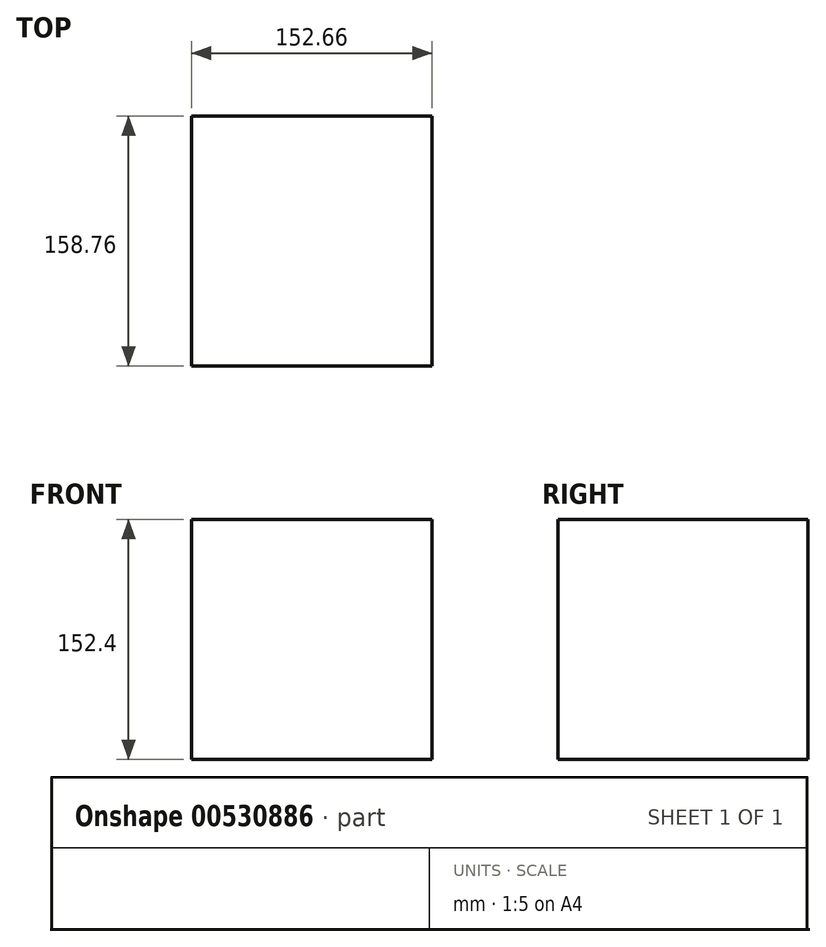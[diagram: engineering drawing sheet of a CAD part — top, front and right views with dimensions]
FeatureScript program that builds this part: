
annotation { "Feature Type Name" : "Feature", "Feature Type Description" : "" }
export const myFeature = defineFeature(function(context is Context, id is Id, definition is map)
    precondition{}
    {
        {
            var Q0;
            Q0=qCreatedBy(makeId("Top.planeOp"),FACE);
            var sketch = newSketch(context, id + "F0", { "sketchPlane" : qUnion([Q0])});
            skLineSegment(sketch, "E0.bottom", {"start": v(76.33, -79.37) * mm, "end": v(-76.33, -79.38) * mm});
            skLineSegment(sketch, "E0.top", {"start": v(76.33, 79.38) * mm, "end": v(-76.33, 79.37) * mm});
            skLineSegment(sketch, "E0.left", {"start": v(76.33, -79.37) * mm, "end": v(76.33, 79.38) * mm});
            skLineSegment(sketch, "E0.right", {"start": v(-76.33, -79.38) * mm, "end": v(-76.33, 79.37) * mm});
            skPoint(sketch, "E0.middle", {"position": v(0, 0) * mm});
            skSolve(sketch);
        }
        {
            var Q0;
            Q0=makeQuery(id+"F0.imprint","IMPRINT",FACE,{"disambiguationData":[TD([[makeQuery(id+"F0.imprint","IMPRINT",EDGE,{"derivedFrom":sQuery(id+"F0.wireOp",EDGE,"E0.bottom")}),-1.0]])]});
            extrude(context, id + "F1", {"entities" : qUnion([Q0]), "depth" : 152.4 * mm, "offsetDistance" : 25.4 * mm});
        }
    });
